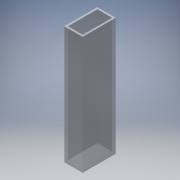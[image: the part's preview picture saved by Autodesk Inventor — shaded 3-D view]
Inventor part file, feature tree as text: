
AUTODESK INVENTOR PART (.ipt)
format: ipt  version: 2016 (Build 200138000, 138)  size: 104,448 bytes
history: native  units: mm
features: extrude x2, sketch x2
ambient origin geometry x8: Origin, YZ Plane, XZ Plane, XY Plane, X Axis, Y Axis, Z Axis, Center Point
bodies: Solid1 (feature_tree)
feature tree (4):
  extrude  "Extrusion1"  Depth=12.5mm
  extrude  "Extrusion2"  Depth=10.0mm
  sketch  "Sketch1"  dims[d0=22.5mm d1=12.5mm]
  sketch  "Sketch2"  dims[d2=80.0mm d3=0.0mm d4=10.0mm d5=20.0mm d6=1.25mm d7=1.25mm d8=78.75mm d9=0.0mm]
